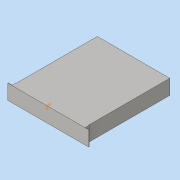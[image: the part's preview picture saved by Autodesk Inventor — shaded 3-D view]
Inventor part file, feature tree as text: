
AUTODESK INVENTOR PART (.ipt)
format: ipt  version: 2016 (Build 200138000, 138)  size: 100,864 bytes
history: native  units: in
note: dims shown in document units (in); Inventor stores cm internally (conversion verified against a paired STEP export)
features: extrude x2, sketch x2, plane x1, mirror x1
ambient origin geometry x8: Origin, YZ Plane, XZ Plane, XY Plane, X Axis, Y Axis, Z Axis, Center Point
bodies: Body1 (feature_tree)
feature tree (6):
  extrude  "Extrusion3"  Depth=20.0in
  plane  "Work Plane3"
  extrude  "Extrusion5"  Depth=1.0in
  mirror  "Mirror1"
  sketch  "Sketch2"  dims[d6=17.0in d7=20.0in]
  sketch  "Sketch4"  dims[d8=3.5in d9=0.0in d13=1.0in d14=1.0in d15=0.104in d16=3.5in d17=0.0in]
